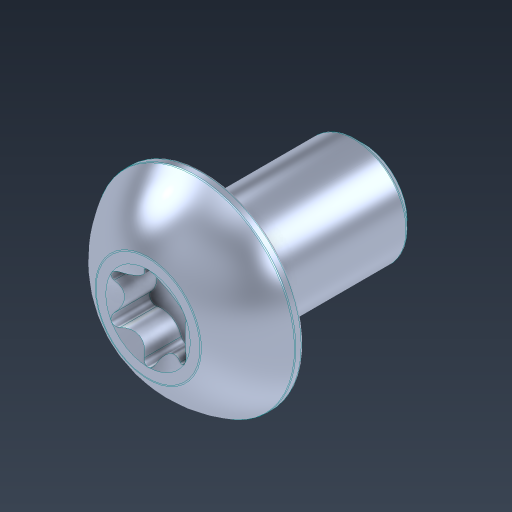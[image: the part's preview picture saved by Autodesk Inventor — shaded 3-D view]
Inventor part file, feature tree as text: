
AUTODESK INVENTOR PART (.ipt)
format: ipt  version: 2024.3 (Build 283343000, 343)  size: 225,792 bytes
history: native  units: in
note: dims shown in document units (in); Inventor stores cm internally (conversion verified against a paired STEP export)
features: fillet x1
ambient origin geometry x8: Origin, YZ Plane, XZ Plane, XY Plane, X Axis, Y Axis, Z Axis, Center Point
bodies: Solid1 (feature_tree)
feature tree (1):
  fillet  "Fillet1"  [1 undecoded]
note: 1 required parameter value undecoded (feature->parameter linkage not recoverable at this tier; creation-order binding heuristic only, values carry confidence <= 0.55)
